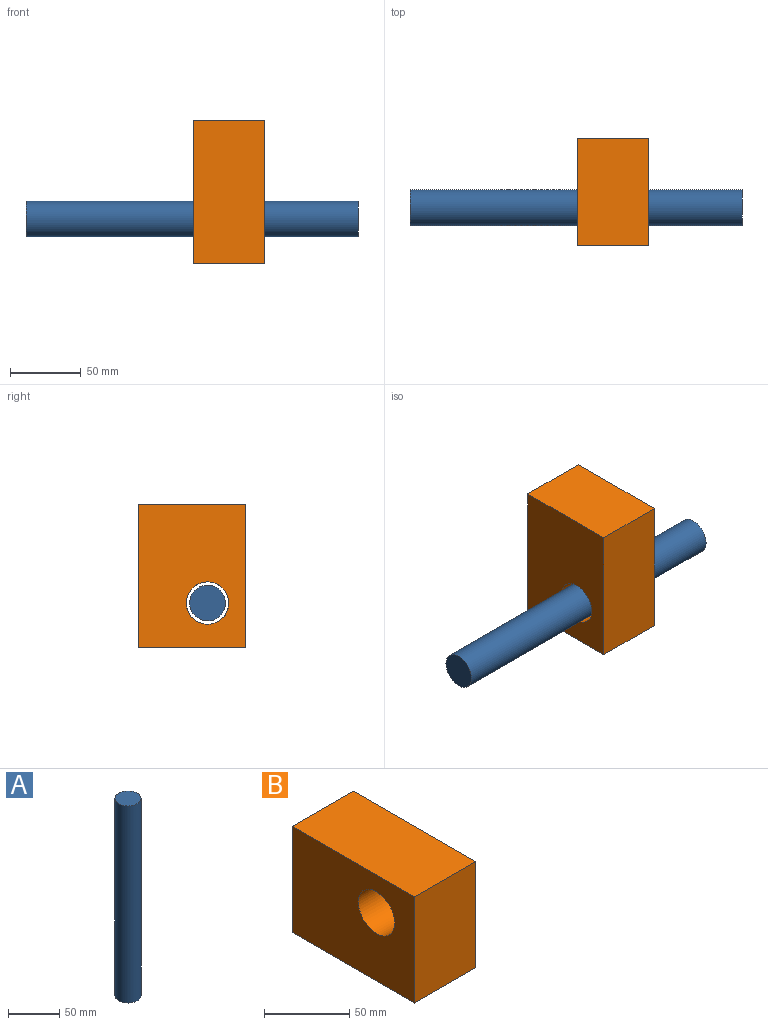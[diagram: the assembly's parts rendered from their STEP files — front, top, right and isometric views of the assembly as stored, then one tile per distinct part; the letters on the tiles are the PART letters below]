
ASSEMBLY  parts=2 mates=2
PART A: 3 faces, bbox 25.4x25.4x235.5 mm
  f0: cylinder r=12.7mm len=235.46mm, axis (0,0,-1), area 18788.7mm2, adj f1,f2
  f1: plane 25.4x25.4mm, normal (0,0,1), area 506.7mm2, adj f0
  f2: plane 25.4x25.4mm, normal (0,0,-1), area 506.7mm2, adj f0
PART B: 7 faces, bbox 50.8x101.6x76.2 mm
  f0: plane 101.6x76.2mm, normal (-1,0,0), area 7031.6mm2, adj f1,f3,f4,f5,f6
  f1: plane 76.2x50.8mm, normal (0,-1,0), area 3871mm2, adj f0,f2,f4,f5
  f2: plane 101.6x76.2mm, normal (1,0,0), area 7031.6mm2, adj f1,f3,f4,f5,f6
  f3: plane 76.2x50.8mm, normal (0,1,0), area 3871mm2, adj f0,f2,f4,f5
  f4: plane 101.6x50.8mm, normal (0,0,1), area 5161.3mm2, adj f0,f1,f2,f3
  f5: plane 101.6x50.8mm, normal (0,0,-1), area 5161.3mm2, adj f0,f1,f2,f3
  f6: cylinder r=15.04mm len=50.8mm, axis (1,0,0), area 4799.6mm2, adj f0,f2
PLACE A rot(axis=(0.51,-0.69,-0.51),110.9deg) t=(91.6,71.59,-30.63)mm
PLACE B rot(axis=(1,0,0),90deg) t=(0,38.1,50.8)mm
MATE cylindrical A.f0 <-> B.f6  axis (1,0,0) through (-26.13,-11.05,31.59)mm
MATE planar B.f2 <-> B.f4  axis (1,0,0) through (25.4,1.12,52.74)mm
